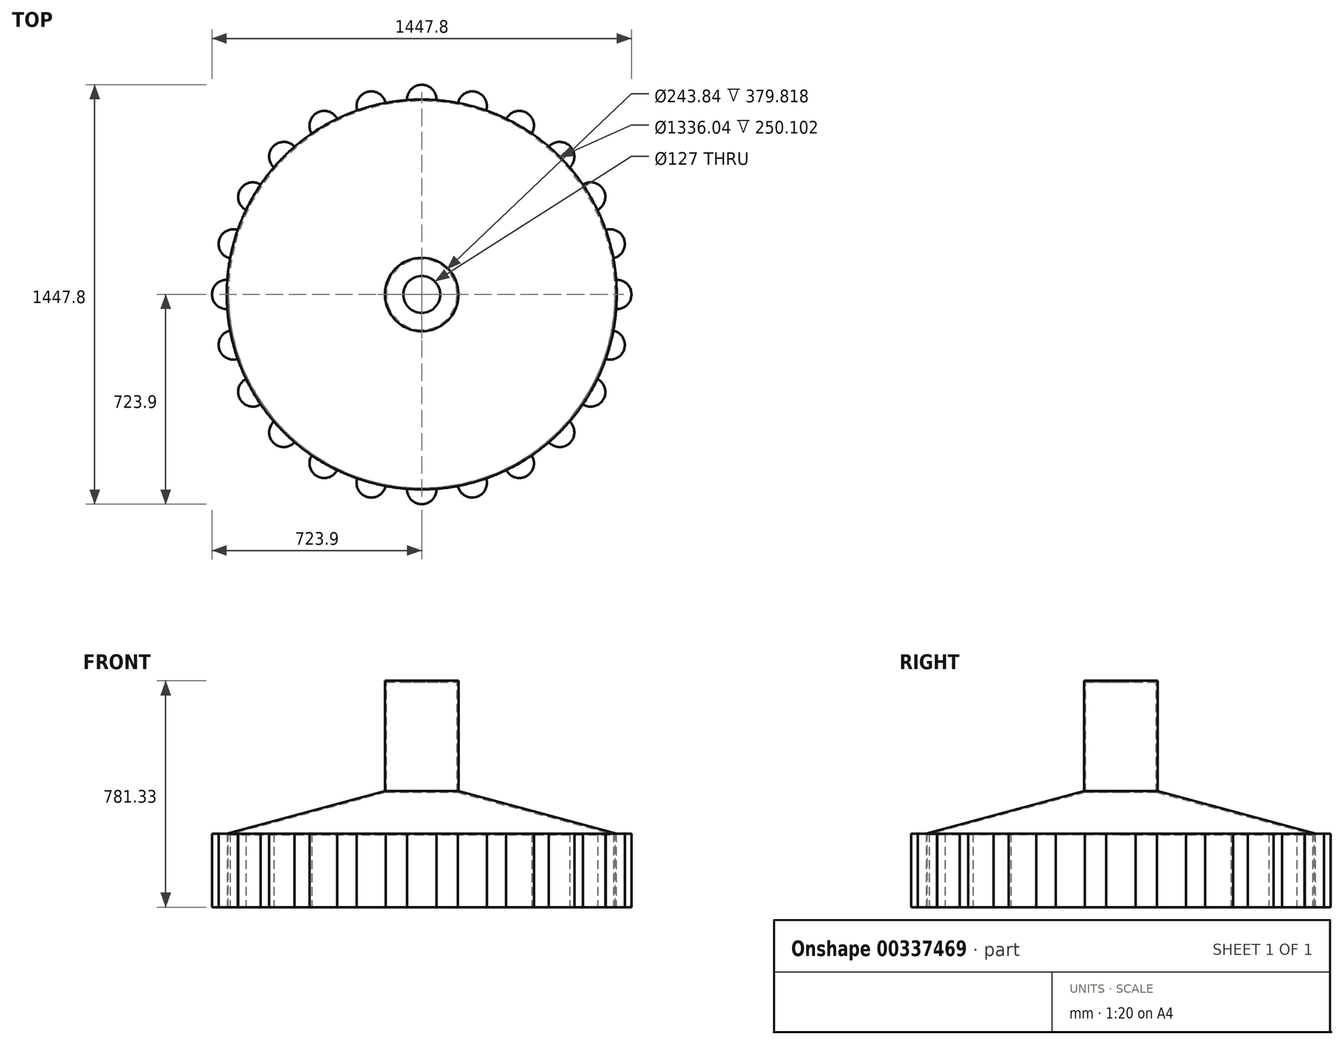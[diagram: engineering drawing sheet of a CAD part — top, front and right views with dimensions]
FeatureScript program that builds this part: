
annotation { "Feature Type Name" : "Feature", "Feature Type Description" : "" }
export const myFeature = defineFeature(function(context is Context, id is Id, definition is map)
    precondition{}
    {
        {
            var Q0;
            Q0=qCreatedBy(makeId("Front.planeOp"),FACE);
            var sketch = newSketch(context, id + "F0", { "sketchPlane" : qUnion([Q0])});
            skLineSegment(sketch, "E0", {"start": v(0, 0) * mm, "end": v(-673.1, 0) * mm});
            skLineSegment(sketch, "E1", {"start": v(-673.1, 0) * mm, "end": v(-673.1, 254) * mm});
            skLineSegment(sketch, "E2", {"start": v(-673.1, 254) * mm, "end": v(-127, 400.33) * mm});
            skLineSegment(sketch, "E3", {"start": v(0, 0) * mm, "end": v(0, 577.47) * mm, "construction": true});
            skLineSegment(sketch, "E4", {"start": v(-127, 400.33) * mm, "end": v(-127, 781.33) * mm});
            skLineSegment(sketch, "E5", {"start": v(-127, 781.33) * mm, "end": v(0, 781.33) * mm});
            skLineSegment(sketch, "E6", {"start": v(0, 781.33) * mm, "end": v(0, 0) * mm});
            skSolve(sketch);
        }
        {
            var Q0;
            Q0=makeQuery(id+"F0.imprint","IMPRINT",FACE,{"disambiguationData":[TD([[makeQuery(id+"F0.imprint","IMPRINT",EDGE,{"derivedFrom":sQuery(id+"F0.wireOp",EDGE,"E0")}),-1.0]])]});
            var Q1;
            Q1=sQuery(id+"F0.wireOp",EDGE,"E6");
            revolve(context, id + "F1", {"entities" : qUnion([Q0]), "axis" : qUnion([Q1]), "revolveType" : RevolveType.FULL});
        }
        {
            var Q0;
            Q0=makeQuery(id+"F1.opRevolve","SWEPT_FACE",FACE,{"disambiguationData":[OSD([sQuery(id+"F0.wireOp",EDGE,"E0")])]});
            shell(context, id + "F2", {"entities" : qUnion([Q0]), "thickness" : 5.08 * mm});
        }
        {
            var Q0;
            Q0=qCreatedBy(makeId("Top.planeOp"),FACE);
            var sketch = newSketch(context, id + "F3", { "sketchPlane" : qUnion([Q0])});
            skCircle(sketch, "E7", {"center": v(0, 0) * mm, "radius": 63.5 * mm});
            skSolve(sketch);
        }
        {
            var Q0;
            Q0 = qSketchRegion(id + "F3", true);
            extrude(context, id + "F4", {"entities" : qUnion([Q0]), "operationType" : NewBodyOperationType.REMOVE, "endBound" : BoundingType.THROUGH_ALL, "depth" : 25.4 * mm});
        }
        {
            var Q0;
            Q0=makeQuery(id+"F1.opRevolve","SWEPT_FACE",FACE,{"disambiguationData":[OSD([sQuery(id+"F0.wireOp",EDGE,"E0")])]});
            var sketch = newSketch(context, id + "F5", { "sketchPlane" : qUnion([Q0])});
            skLineSegment(sketch, "E8", {"start": v(-44.13, 0) * mm, "end": v(-818.67, 0) * mm, "construction": true});
            skArc(sketch, "E9", {"start": v(-671.18, 50.76) * mm, "mid": v(-723.9, 0) * mm, "end": v(-671.18, -50.76) * mm});
            skArc(sketch, "E10", {"start": v(-671.18, 50.76) * mm, "mid": v(-673.1, 0) * mm, "end": v(-671.18, -50.76) * mm});
            skSolve(sketch);
        }
        {
            var Q0;
            Q0=makeQuery(id+"F5.imprint","IMPRINT",FACE,{"disambiguationData":[TD([[makeQuery(id+"F5.imprint","IMPRINT",EDGE,{"derivedFrom":sQuery(id+"F5.wireOp",EDGE,"E9")}),1.0]])]});
            extrude(context, id + "F6", {"entities" : qUnion([Q0]), "operationType" : NewBodyOperationType.ADD, "oppositeDirection" : true, "depth" : 254 * mm});
        }
        {
            var Q0;
            Q0=makeQuery(id+"F1.opRevolve","SWEPT_BODY",BODY,{"disambiguationData":[OSD([sQuery(id+"F0.wireOp",EDGE,"E0"),sQuery(id+"F0.wireOp",EDGE,"E1"),sQuery(id+"F0.wireOp",EDGE,"E2"),sQuery(id+"F0.wireOp",EDGE,"E4"),sQuery(id+"F0.wireOp",EDGE,"E5"),sQuery(id+"F0.wireOp",EDGE,"E6")])]});
            var Q1;
            Q1=makeQuery(id+"F4.boolean.opBoolean","INTERSECT",EDGE,{"derivedFrom":[makeQuery(id+"F1.opRevolve","SWEPT_FACE",FACE,{"disambiguationData":[OSD([sQuery(id+"F0.wireOp",EDGE,"E5")])]}),makeQuery(id+"F4.opExtrude","SWEPT_FACE",FACE,{"disambiguationData":[OSD([sQuery(id+"F3.wireOp",EDGE,"E7")])]})]});
            circularPattern(context, id + "F7", {"operationType" : NewBodyOperationType.ADD, "entities" : qUnion([Q0]), "axis" : qUnion([Q1]), "angle" : 360 * degree, "instanceCount" : 24, "equalSpace" : true});
        }
    });
